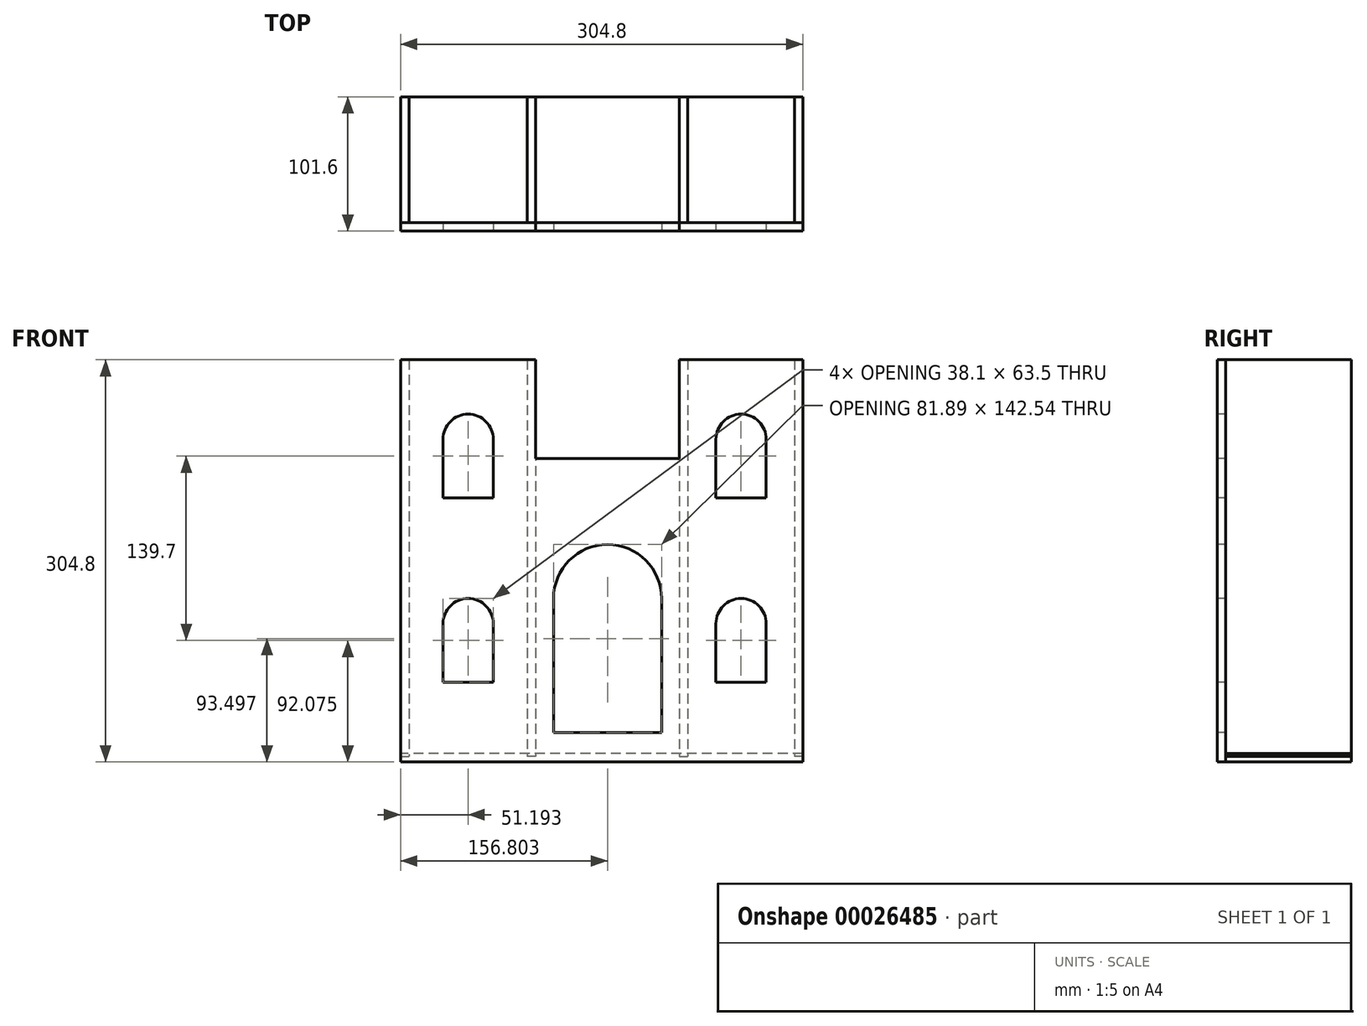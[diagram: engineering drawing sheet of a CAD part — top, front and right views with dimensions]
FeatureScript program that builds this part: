
annotation { "Feature Type Name" : "Feature", "Feature Type Description" : "" }
export const myFeature = defineFeature(function(context is Context, id is Id, definition is map)
    precondition{}
    {
        {
            var Q0;
            Q0=qCreatedBy(makeId("Front.planeOp"),FACE);
            var sketch = newSketch(context, id + "F0", { "sketchPlane" : qUnion([Q0])});
            skLineSegment(sketch, "E0.rect.bottom", {"start": v(-152.4, -152.4) * mm, "end": v(152.4, -152.4) * mm});
            skLineSegment(sketch, "E0.rect.top", {"start": v(-152.4, 152.4) * mm, "end": v(-50.01, 152.4) * mm});
            skLineSegment(sketch, "E0.rect.left", {"start": v(-152.4, -152.4) * mm, "end": v(-152.4, 152.4) * mm});
            skLineSegment(sketch, "E0.rect.right", {"start": v(152.4, -152.4) * mm, "end": v(152.4, 152.4) * mm});
            skPoint(sketch, "E0.rect.middle", {"position": v(0, 0) * mm});
            skLineSegment(sketch, "E1", {"start": v(-36.54, -130.18) * mm, "end": v(45.35, -130.18) * mm});
            skLineSegment(sketch, "E2", {"start": v(45.35, -130.18) * mm, "end": v(45.35, -28.58) * mm});
            skLineSegment(sketch, "E3", {"start": v(-36.54, -130.18) * mm, "end": v(-36.54, -28.58) * mm});
            skArc(sketch, "E4", {"start": v(45.35, -28.58) * mm, "mid": v(4.4, 12.37) * mm, "end": v(-36.54, -28.58) * mm});
            skLineSegment(sketch, "E5", {"start": v(-120.26, -47.63) * mm, "end": v(-120.26, -92.08) * mm});
            skLineSegment(sketch, "E6", {"start": v(-120.26, -92.08) * mm, "end": v(-82.16, -92.08) * mm});
            skLineSegment(sketch, "E7", {"start": v(-82.16, -92.08) * mm, "end": v(-82.16, -47.63) * mm});
            skArc(sketch, "E8", {"start": v(-82.16, -47.63) * mm, "mid": v(-101.2, -28.58) * mm, "end": v(-120.26, -47.63) * mm});
            skLineSegment(sketch, "E9", {"start": v(-120.26, 47.62) * mm, "end": v(-82.16, 47.62) * mm});
            skLineSegment(sketch, "E10", {"start": v(-82.16, 47.62) * mm, "end": v(-82.16, 92.07) * mm});
            skLineSegment(sketch, "E11", {"start": v(-120.26, 47.62) * mm, "end": v(-120.26, 92.07) * mm});
            skArc(sketch, "E12", {"start": v(-82.16, 92.07) * mm, "mid": v(-101.2, 111.12) * mm, "end": v(-120.26, 92.07) * mm});
            skLineSegment(sketch, "E13", {"start": v(86.56, -92.08) * mm, "end": v(124.66, -92.08) * mm});
            skLineSegment(sketch, "E14", {"start": v(124.66, -92.07) * mm, "end": v(124.66, -47.63) * mm});
            skLineSegment(sketch, "E15", {"start": v(86.56, -92.07) * mm, "end": v(86.56, -47.63) * mm});
            skArc(sketch, "E16", {"start": v(124.66, -47.63) * mm, "mid": v(105.61, -28.57) * mm, "end": v(86.56, -47.63) * mm});
            skLineSegment(sketch, "E17", {"start": v(86.56, 92.07) * mm, "end": v(86.56, 47.63) * mm});
            skLineSegment(sketch, "E18", {"start": v(86.56, 47.62) * mm, "end": v(124.66, 47.62) * mm});
            skLineSegment(sketch, "E19", {"start": v(124.66, 47.63) * mm, "end": v(124.66, 92.07) * mm});
            skArc(sketch, "E20", {"start": v(124.66, 92.07) * mm, "mid": v(105.61, 111.13) * mm, "end": v(86.56, 92.07) * mm});
            skLineSegment(sketch, "E21", {"start": v(-50.01, 152.4) * mm, "end": v(-50.01, 77.54) * mm});
            skLineSegment(sketch, "E22", {"start": v(-50.01, 77.54) * mm, "end": v(58.82, 77.54) * mm});
            skLineSegment(sketch, "E23", {"start": v(58.82, 77.54) * mm, "end": v(58.82, 152.4) * mm});
            skLineSegment(sketch, "E24.trimOffspring", {"start": v(58.82, 152.4) * mm, "end": v(152.4, 152.4) * mm});
            skLineSegment(sketch, "E25", {"start": v(4.4, 77.54) * mm, "end": v(4.4, -152.4) * mm, "construction": true});
            skLineSegment(sketch, "E26", {"start": v(-101.2, 152.4) * mm, "end": v(-101.2, -152.4) * mm, "construction": true});
            skLineSegment(sketch, "E27", {"start": v(105.61, 152.4) * mm, "end": v(105.61, -152.4) * mm, "construction": true});
            skSolve(sketch);
        }
        {
            var Q0;
            Q0=makeQuery(id+"F0.imprint","IMPRINT",FACE,{"disambiguationData":[TD([[makeQuery(id+"F0.imprint","IMPRINT",EDGE,{"derivedFrom":sQuery(id+"F0.wireOp",EDGE,"E0.rect.bottom")}),1.0]])]});
            extrude(context, id + "F1", {"entities" : qUnion([Q0]), "oppositeDirection" : true, "depth" : 6.35 * mm});
        }
        {
            var Q0;
            Q0=makeQuery(id+"F1.opExtrude","CAP_FACE",FACE,{"disambiguationData":[OSD([sQuery(id+"F0.wireOp",EDGE,"E0.rect.bottom"),sQuery(id+"F0.wireOp",EDGE,"E0.rect.top"),sQuery(id+"F0.wireOp",EDGE,"E0.rect.left"),sQuery(id+"F0.wireOp",EDGE,"E0.rect.right"),sQuery(id+"F0.wireOp",EDGE,"E1"),sQuery(id+"F0.wireOp",EDGE,"E2"),sQuery(id+"F0.wireOp",EDGE,"E3"),sQuery(id+"F0.wireOp",EDGE,"E4"),sQuery(id+"F0.wireOp",EDGE,"E5"),sQuery(id+"F0.wireOp",EDGE,"E6"),sQuery(id+"F0.wireOp",EDGE,"E7"),sQuery(id+"F0.wireOp",EDGE,"E8"),sQuery(id+"F0.wireOp",EDGE,"E9"),sQuery(id+"F0.wireOp",EDGE,"E10"),sQuery(id+"F0.wireOp",EDGE,"E11"),sQuery(id+"F0.wireOp",EDGE,"E12"),sQuery(id+"F0.wireOp",EDGE,"E13"),sQuery(id+"F0.wireOp",EDGE,"E14"),sQuery(id+"F0.wireOp",EDGE,"E15"),sQuery(id+"F0.wireOp",EDGE,"E16"),sQuery(id+"F0.wireOp",EDGE,"E17"),sQuery(id+"F0.wireOp",EDGE,"E18"),sQuery(id+"F0.wireOp",EDGE,"E19"),sQuery(id+"F0.wireOp",EDGE,"E20"),sQuery(id+"F0.wireOp",EDGE,"E21"),sQuery(id+"F0.wireOp",EDGE,"E22"),sQuery(id+"F0.wireOp",EDGE,"E23"),sQuery(id+"F0.wireOp",EDGE,"E24.trimOffspring")])],"isStart":false});
            var sketch = newSketch(context, id + "F2", { "sketchPlane" : qUnion([Q0])});
            skLineSegment(sketch, "E28.bottom", {"start": v(-152.4, -152.4) * mm, "end": v(152.4, -152.4) * mm});
            skLineSegment(sketch, "E28.top", {"start": v(-152.4, -146.05) * mm, "end": v(152.4, -146.05) * mm});
            skLineSegment(sketch, "E28.left", {"start": v(-152.4, -152.4) * mm, "end": v(-152.4, -146.05) * mm});
            skLineSegment(sketch, "E28.right", {"start": v(152.4, -152.4) * mm, "end": v(152.4, -146.05) * mm});
            skSolve(sketch);
        }
        {
            var Q0;
            Q0=makeQuery(id+"F2.imprint","IMPRINT",FACE,{"disambiguationData":[TD([[makeQuery(id+"F2.imprint","IMPRINT",EDGE,{"derivedFrom":sQuery(id+"F2.wireOp",EDGE,"E28.bottom")}),-1.0]])]});
            extrude(context, id + "F3", {"entities" : qUnion([Q0]), "depth" : 95.25 * mm});
        }
        {
            var Q0;
            Q0=makeQuery(id+"F1.opExtrude","CAP_FACE",FACE,{"disambiguationData":[OSD([sQuery(id+"F0.wireOp",EDGE,"E0.rect.bottom"),sQuery(id+"F0.wireOp",EDGE,"E0.rect.top"),sQuery(id+"F0.wireOp",EDGE,"E0.rect.left"),sQuery(id+"F0.wireOp",EDGE,"E0.rect.right"),sQuery(id+"F0.wireOp",EDGE,"E1"),sQuery(id+"F0.wireOp",EDGE,"E2"),sQuery(id+"F0.wireOp",EDGE,"E3"),sQuery(id+"F0.wireOp",EDGE,"E4"),sQuery(id+"F0.wireOp",EDGE,"E5"),sQuery(id+"F0.wireOp",EDGE,"E6"),sQuery(id+"F0.wireOp",EDGE,"E7"),sQuery(id+"F0.wireOp",EDGE,"E8"),sQuery(id+"F0.wireOp",EDGE,"E9"),sQuery(id+"F0.wireOp",EDGE,"E10"),sQuery(id+"F0.wireOp",EDGE,"E11"),sQuery(id+"F0.wireOp",EDGE,"E12"),sQuery(id+"F0.wireOp",EDGE,"E13"),sQuery(id+"F0.wireOp",EDGE,"E14"),sQuery(id+"F0.wireOp",EDGE,"E15"),sQuery(id+"F0.wireOp",EDGE,"E16"),sQuery(id+"F0.wireOp",EDGE,"E17"),sQuery(id+"F0.wireOp",EDGE,"E18"),sQuery(id+"F0.wireOp",EDGE,"E19"),sQuery(id+"F0.wireOp",EDGE,"E20"),sQuery(id+"F0.wireOp",EDGE,"E21"),sQuery(id+"F0.wireOp",EDGE,"E22"),sQuery(id+"F0.wireOp",EDGE,"E23"),sQuery(id+"F0.wireOp",EDGE,"E24.trimOffspring")])],"isStart":false});
            var sketch = newSketch(context, id + "F4", { "sketchPlane" : qUnion([Q0])});
            skLineSegment(sketch, "E29.bottom", {"start": v(-152.4, 152.4) * mm, "end": v(-146.05, 152.4) * mm});
            skLineSegment(sketch, "E29.top", {"start": v(-152.4, -148.16) * mm, "end": v(-146.05, -148.16) * mm});
            skLineSegment(sketch, "E29.left", {"start": v(-152.4, 152.4) * mm, "end": v(-152.4, -148.16) * mm});
            skLineSegment(sketch, "E29.right", {"start": v(-146.05, 152.4) * mm, "end": v(-146.05, -148.16) * mm});
            skLineSegment(sketch, "E30.bottom", {"start": v(-58.82, 152.4) * mm, "end": v(-65.17, 152.4) * mm});
            skLineSegment(sketch, "E30.top", {"start": v(-58.82, -148.16) * mm, "end": v(-65.17, -148.16) * mm});
            skLineSegment(sketch, "E30.left", {"start": v(-58.82, 152.4) * mm, "end": v(-58.82, -148.16) * mm});
            skLineSegment(sketch, "E30.right", {"start": v(-65.17, 152.4) * mm, "end": v(-65.17, -148.16) * mm});
            skLineSegment(sketch, "E31.bottom", {"start": v(50.01, 152.4) * mm, "end": v(56.36, 152.4) * mm});
            skLineSegment(sketch, "E31.top", {"start": v(50.01, -148.16) * mm, "end": v(56.36, -148.16) * mm});
            skLineSegment(sketch, "E31.left", {"start": v(50.01, 152.4) * mm, "end": v(50.01, -148.16) * mm});
            skLineSegment(sketch, "E31.right", {"start": v(56.36, 152.4) * mm, "end": v(56.36, -148.16) * mm});
            skLineSegment(sketch, "E32.bottom", {"start": v(152.4, 152.4) * mm, "end": v(146.05, 152.4) * mm});
            skLineSegment(sketch, "E32.top", {"start": v(152.4, -148.16) * mm, "end": v(146.05, -148.16) * mm});
            skLineSegment(sketch, "E32.left", {"start": v(152.4, 152.4) * mm, "end": v(152.4, -148.16) * mm});
            skLineSegment(sketch, "E32.right", {"start": v(146.05, 152.4) * mm, "end": v(146.05, -148.16) * mm});
            skSolve(sketch);
        }
        {
            var Q0;
            Q0=makeQuery(id+"F4.imprint","IMPRINT",FACE,{"disambiguationData":[TD([[makeQuery(id+"F4.imprint","IMPRINT",EDGE,{"derivedFrom":sQuery(id+"F4.wireOp",EDGE,"E29.bottom")}),1.0]])]});
            var Q1;
            {var subQ1=sQuery(id+"F4.wireOp",EDGE,"E30.bottom");Q1=makeQuery(id+"F4.imprint","IMPRINT",FACE,{"disambiguationData":[TD([[makeQuery(id+"F4.imprint","IMPRINT",EDGE,{"derivedFrom":subQ1}),1.0]])]});}
            var Q2;
            {var subQ2=sQuery(id+"F4.wireOp",EDGE,"E31.bottom");Q2=makeQuery(id+"F4.imprint","IMPRINT",FACE,{"disambiguationData":[TD([[makeQuery(id+"F4.imprint","IMPRINT",EDGE,{"derivedFrom":subQ2}),1.0]])]});}
            var Q3;
            Q3=makeQuery(id+"F4.imprint","IMPRINT",FACE,{"disambiguationData":[TD([[makeQuery(id+"F4.imprint","IMPRINT",EDGE,{"derivedFrom":sQuery(id+"F4.wireOp",EDGE,"E32.bottom")}),1.0]])]});
            extrude(context, id + "F5", {"entities" : qUnion([Q0, Q1, Q2, Q3]), "depth" : 95.25 * mm});
        }
        {
            var Q0;
            Q0=makeQuery(id+"F5.opExtrude","SWEPT_BODY",BODY,{"disambiguationData":[OSD([sQuery(id+"F4.wireOp",EDGE,"E29.bottom"),sQuery(id+"F4.wireOp",EDGE,"E29.top"),sQuery(id+"F4.wireOp",EDGE,"E29.left"),sQuery(id+"F4.wireOp",EDGE,"E29.right")])]});
            var Q1;
            Q1=makeQuery(id+"F3.opExtrude","SWEPT_BODY",BODY,{"disambiguationData":[OSD([sQuery(id+"F2.wireOp",EDGE,"E28.bottom"),sQuery(id+"F2.wireOp",EDGE,"E28.top"),sQuery(id+"F2.wireOp",EDGE,"E28.left"),sQuery(id+"F2.wireOp",EDGE,"E28.right")])]});
            booleanBodies(context, id + "F6", {"operationType" : BooleanOperationType.INTERSECTION, "tools" : qUnion([Q0, Q1]), "keepTools" : true});
        }
    });
